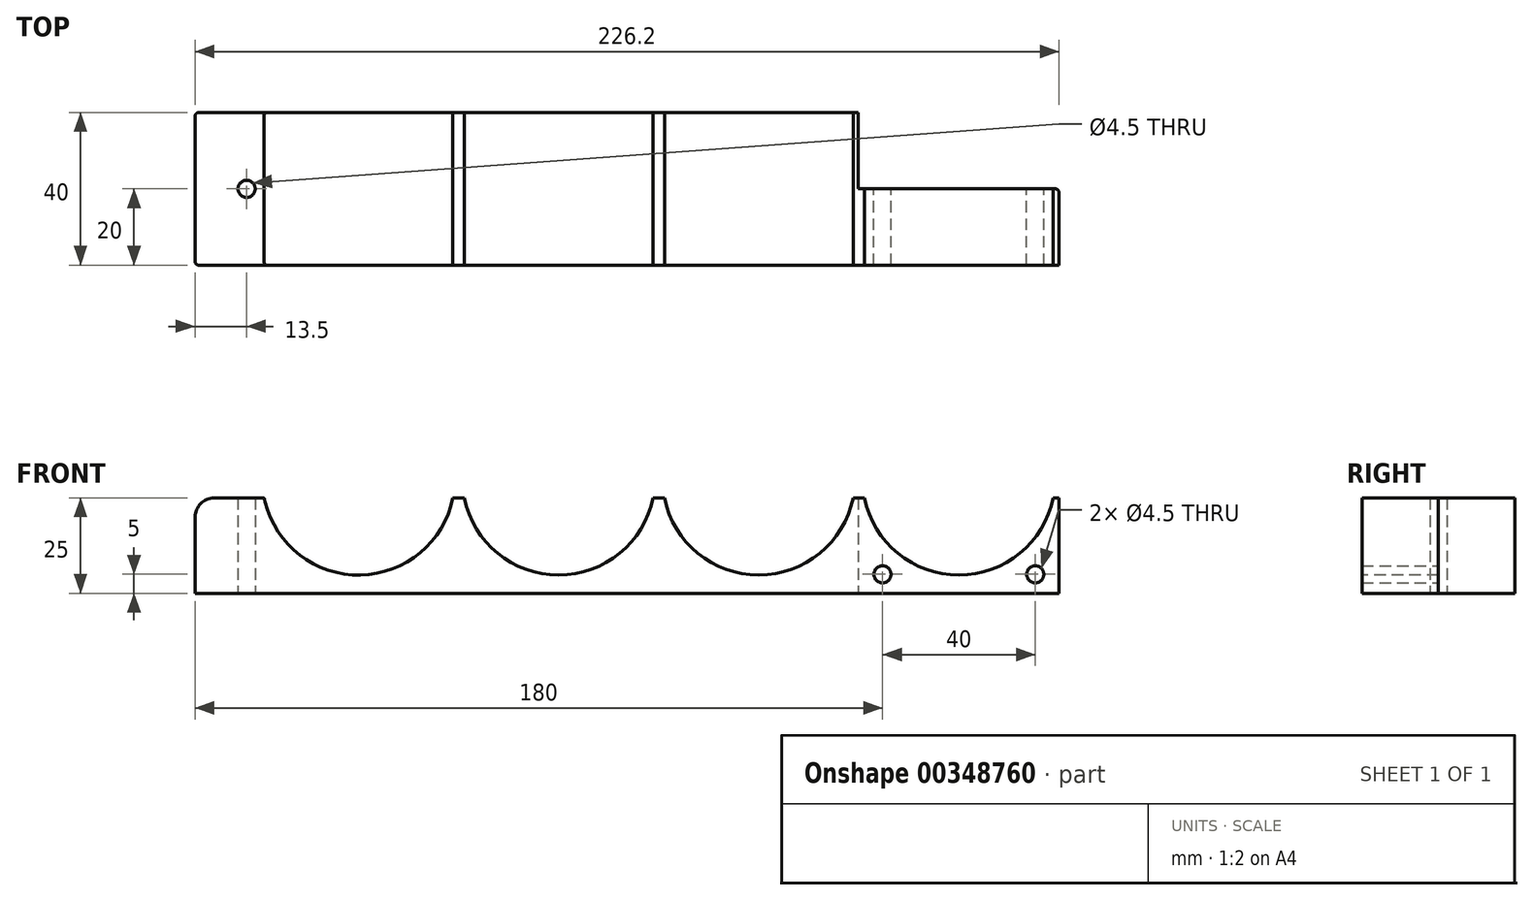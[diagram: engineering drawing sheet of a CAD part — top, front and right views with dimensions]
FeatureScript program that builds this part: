
annotation { "Feature Type Name" : "Feature", "Feature Type Description" : "" }
export const myFeature = defineFeature(function(context is Context, id is Id, definition is map)
    precondition{}
    {
        {
            var Q0;
            Q0=qCreatedBy(makeId("Top.planeOp"),FACE);
            var sketch = newSketch(context, id + "F0", { "sketchPlane" : qUnion([Q0])});
            skLineSegment(sketch, "E0.bottom", {"start": v(113.1, -20) * mm, "end": v(-113.1, -20) * mm});
            skLineSegment(sketch, "E0.top", {"start": v(60.5, 20) * mm, "end": v(-113.1, 20) * mm});
            skLineSegment(sketch, "E0.left", {"start": v(113.1, -20) * mm, "end": v(113.1, 0) * mm});
            skLineSegment(sketch, "E0.right", {"start": v(-113.1, -20) * mm, "end": v(-113.1, 20) * mm});
            skPoint(sketch, "E0.middle", {"position": v(0, 0) * mm});
            skLineSegment(sketch, "E1", {"start": v(60.5, 20) * mm, "end": v(60.5, 0) * mm});
            skLineSegment(sketch, "E2", {"start": v(60.5, 0) * mm, "end": v(113.1, 0) * mm});
            skPoint(sketch, "E3.orphan", {"position": v(113.1, 20) * mm});
            skCircle(sketch, "E4", {"center": v(-99.6, 0) * mm, "radius": 2.25 * mm});
            skSolve(sketch);
        }
        {
            var Q0;
            Q0=makeQuery(id+"F0.imprint","IMPRINT",FACE,{"disambiguationData":[TD([[makeQuery(id+"F0.imprint","IMPRINT",EDGE,{"derivedFrom":sQuery(id+"F0.wireOp",EDGE,"E0.bottom")}),-1.0]])]});
            extrude(context, id + "F1", {"entities" : qUnion([Q0]), "depth" : 25 * mm});
        }
        {
            var Q0;
            Q0=makeQuery(id+"F1.opExtrude","SWEPT_FACE",FACE,{"disambiguationData":[OSD([sQuery(id+"F0.wireOp",EDGE,"E0.bottom")])]});
            var sketch = newSketch(context, id + "F2", { "sketchPlane" : qUnion([Q0])});
            skLineSegment(sketch, "E5", {"start": v(-113.1, 30) * mm, "end": v(113.1, 30) * mm, "construction": true});
            skLineSegment(sketch, "E6", {"start": v(-95.5, 30) * mm, "end": v(-45.1, 30) * mm});
            skArc(sketch, "E7", {"start": v(-95.5, 30) * mm, "mid": v(-70.3, 4.8) * mm, "end": v(-45.1, 30) * mm});
            skArc(sketch, "E8.1.0.0", {"start": v(-43.1, 30) * mm, "mid": v(-17.9, 4.8) * mm, "end": v(7.3, 30) * mm});
            skArc(sketch, "E8.2.0.0", {"start": v(9.3, 30) * mm, "mid": v(34.5, 4.8) * mm, "end": v(59.7, 30) * mm});
            skArc(sketch, "E8.3.0.0", {"start": v(61.7, 30) * mm, "mid": v(86.9, 4.8) * mm, "end": v(112.1, 30) * mm});
            skLineSegment(sketch, "E8.direction1", {"start": v(-95.5, 30) * mm, "end": v(-43.1, 30) * mm, "construction": true});
            skLineSegment(sketch, "E9", {"start": v(-43.1, 30) * mm, "end": v(7.3, 30) * mm});
            skLineSegment(sketch, "E10", {"start": v(9.3, 30) * mm, "end": v(59.7, 30) * mm});
            skLineSegment(sketch, "E11", {"start": v(61.7, 30) * mm, "end": v(112.1, 30) * mm});
            skSolve(sketch);
        }
        {
            var Q0;
            Q0 = qSketchRegion(id + "F2", true);
            extrude(context, id + "F3", {"entities" : qUnion([Q0]), "operationType" : NewBodyOperationType.REMOVE, "endBound" : BoundingType.THROUGH_ALL, "oppositeDirection" : true, "depth" : 25 * mm});
        }
        {
            var Q0;
            Q0=makeQuery(id+"F1.opExtrude","SWEPT_FACE",FACE,{"disambiguationData":[OSD([sQuery(id+"F0.wireOp",EDGE,"E2")])]});
            var sketch = newSketch(context, id + "F4", { "sketchPlane" : qUnion([Q0])});
            skCircle(sketch, "E12", {"center": v(-66.9, 5) * mm, "radius": 2.25 * mm});
            skCircle(sketch, "E13", {"center": v(-106.9, 5) * mm, "radius": 2.25 * mm});
            skSolve(sketch);
        }
        {
            var Q0;
            Q0 = qSketchRegion(id + "F4", true);
            extrude(context, id + "F5", {"entities" : qUnion([Q0]), "operationType" : NewBodyOperationType.REMOVE, "endBound" : BoundingType.THROUGH_ALL, "oppositeDirection" : true, "depth" : 25 * mm});
        }
        {
            var Q0;
            Q0=makeQuery(id+"F1.opExtrude","CAP_EDGE",EDGE,{"disambiguationData":[OSD([sQuery(id+"F0.wireOp",EDGE,"E0.right")])],"isStart":false});
            fillet(context, id + "F6", {"entities" : qUnion([Q0]), "radius" : 5 * mm, "tangentPropagation" : true, "allowEdgeOverflow" : false});
        }
        {
            var Q0;
            Q0=makeQuery(id+"F1.opExtrude","SWEPT_EDGE",EDGE,{"disambiguationData":[OSD([sQuery(id+"F0.wireOp",EDGE,"E0.left"),sQuery(id+"F0.wireOp",EDGE,"E2")])]});
            fillet(context, id + "F7", {"entities" : qUnion([Q0]), "radius" : 1 * mm, "tangentPropagation" : true, "allowEdgeOverflow" : false});
        }
        {
            var Q0;
            Q0=makeQuery(id+"F1.opExtrude","SWEPT_EDGE",EDGE,{"disambiguationData":[OSD([sQuery(id+"F0.wireOp",EDGE,"E0.top"),sQuery(id+"F0.wireOp",EDGE,"E0.right")])]});
            var Q1;
            Q1=makeQuery(id+"F6.opFillet","BLEND_EDGE",EDGE,{"blendedFrom":[makeQuery(id+"F1.opExtrude","CAP_EDGE",EDGE,{"disambiguationData":[OSD([sQuery(id+"F0.wireOp",EDGE,"E0.right")])],"isStart":false}),makeQuery(id+"F1.opExtrude","SWEPT_FACE",FACE,{"disambiguationData":[OSD([sQuery(id+"F0.wireOp",EDGE,"E0.top")])]})],"blendedInto":[makeQuery(id+"F1.opExtrude","SWEPT_FACE",FACE,{"disambiguationData":[OSD([sQuery(id+"F0.wireOp",EDGE,"E0.top")])]})]});
            var Q2;
            {var subQ0=sQuery(id+"F0.wireOp",EDGE,"E0.right");var subQ1=sQuery(id+"F0.wireOp",EDGE,"E0.top");Q2=makeQuery(id+"F3.boolean.opBoolean","SPLIT",EDGE,{"disambiguationData":[TD([makeQuery(id+"F1.opExtrude","CAP_FACE",FACE,{"disambiguationData":[OSD([sQuery(id+"F0.wireOp",EDGE,"E0.bottom"),subQ1,sQuery(id+"F0.wireOp",EDGE,"E0.left"),subQ0,sQuery(id+"F0.wireOp",EDGE,"E1"),sQuery(id+"F0.wireOp",EDGE,"E2"),sQuery(id+"F0.wireOp",EDGE,"E4")])],"isStart":false}),makeQuery(id+"F1.opExtrude","SWEPT_FACE",FACE,{"disambiguationData":[OSD([subQ1])]}),makeQuery(id+"F1.opExtrude","SWEPT_FACE",FACE,{"disambiguationData":[OSD([subQ0])]}),makeQuery(id+"F3.opExtrude","SWEPT_FACE",FACE,{"disambiguationData":[OSD([sQuery(id+"F2.wireOp",EDGE,"E7")])]})])],"derivedFrom":makeQuery(id+"F1.opExtrude","CAP_EDGE",EDGE,{"disambiguationData":[OSD([subQ1])],"isStart":false})});}
            var Q3;
            Q3=makeQuery(id+"F1.opExtrude","SWEPT_EDGE",EDGE,{"disambiguationData":[OSD([sQuery(id+"F0.wireOp",EDGE,"E0.bottom"),sQuery(id+"F0.wireOp",EDGE,"E0.right")])]});
            var Q4;
            Q4=makeQuery(id+"F6.opFillet","BLEND_EDGE",EDGE,{"blendedFrom":[makeQuery(id+"F1.opExtrude","CAP_EDGE",EDGE,{"disambiguationData":[OSD([sQuery(id+"F0.wireOp",EDGE,"E0.right")])],"isStart":false}),makeQuery(id+"F1.opExtrude","SWEPT_FACE",FACE,{"disambiguationData":[OSD([sQuery(id+"F0.wireOp",EDGE,"E0.bottom")])]})],"blendedInto":[makeQuery(id+"F1.opExtrude","SWEPT_FACE",FACE,{"disambiguationData":[OSD([sQuery(id+"F0.wireOp",EDGE,"E0.bottom")])]})]});
            var Q5;
            {var subQ0=sQuery(id+"F0.wireOp",EDGE,"E0.bottom");var subQ1=sQuery(id+"F0.wireOp",EDGE,"E0.right");Q5=makeQuery(id+"F3.boolean.opBoolean","SPLIT",EDGE,{"disambiguationData":[TD([makeQuery(id+"F1.opExtrude","SWEPT_FACE",FACE,{"disambiguationData":[OSD([subQ0])]}),makeQuery(id+"F1.opExtrude","CAP_FACE",FACE,{"disambiguationData":[OSD([subQ0,sQuery(id+"F0.wireOp",EDGE,"E0.top"),sQuery(id+"F0.wireOp",EDGE,"E0.left"),subQ1,sQuery(id+"F0.wireOp",EDGE,"E1"),sQuery(id+"F0.wireOp",EDGE,"E2"),sQuery(id+"F0.wireOp",EDGE,"E4")])],"isStart":false}),makeQuery(id+"F1.opExtrude","SWEPT_FACE",FACE,{"disambiguationData":[OSD([subQ1])]}),makeQuery(id+"F3.opExtrude","SWEPT_FACE",FACE,{"disambiguationData":[OSD([sQuery(id+"F2.wireOp",EDGE,"E7")])]})])],"derivedFrom":makeQuery(id+"F1.opExtrude","CAP_EDGE",EDGE,{"disambiguationData":[OSD([subQ0])],"isStart":false})});}
            fillet(context, id + "F8", {"entities" : qUnion([Q0, Q1, Q2, Q3, Q4, Q5]), "radius" : 1 * mm, "tangentPropagation" : true, "allowEdgeOverflow" : false});
        }
    });
